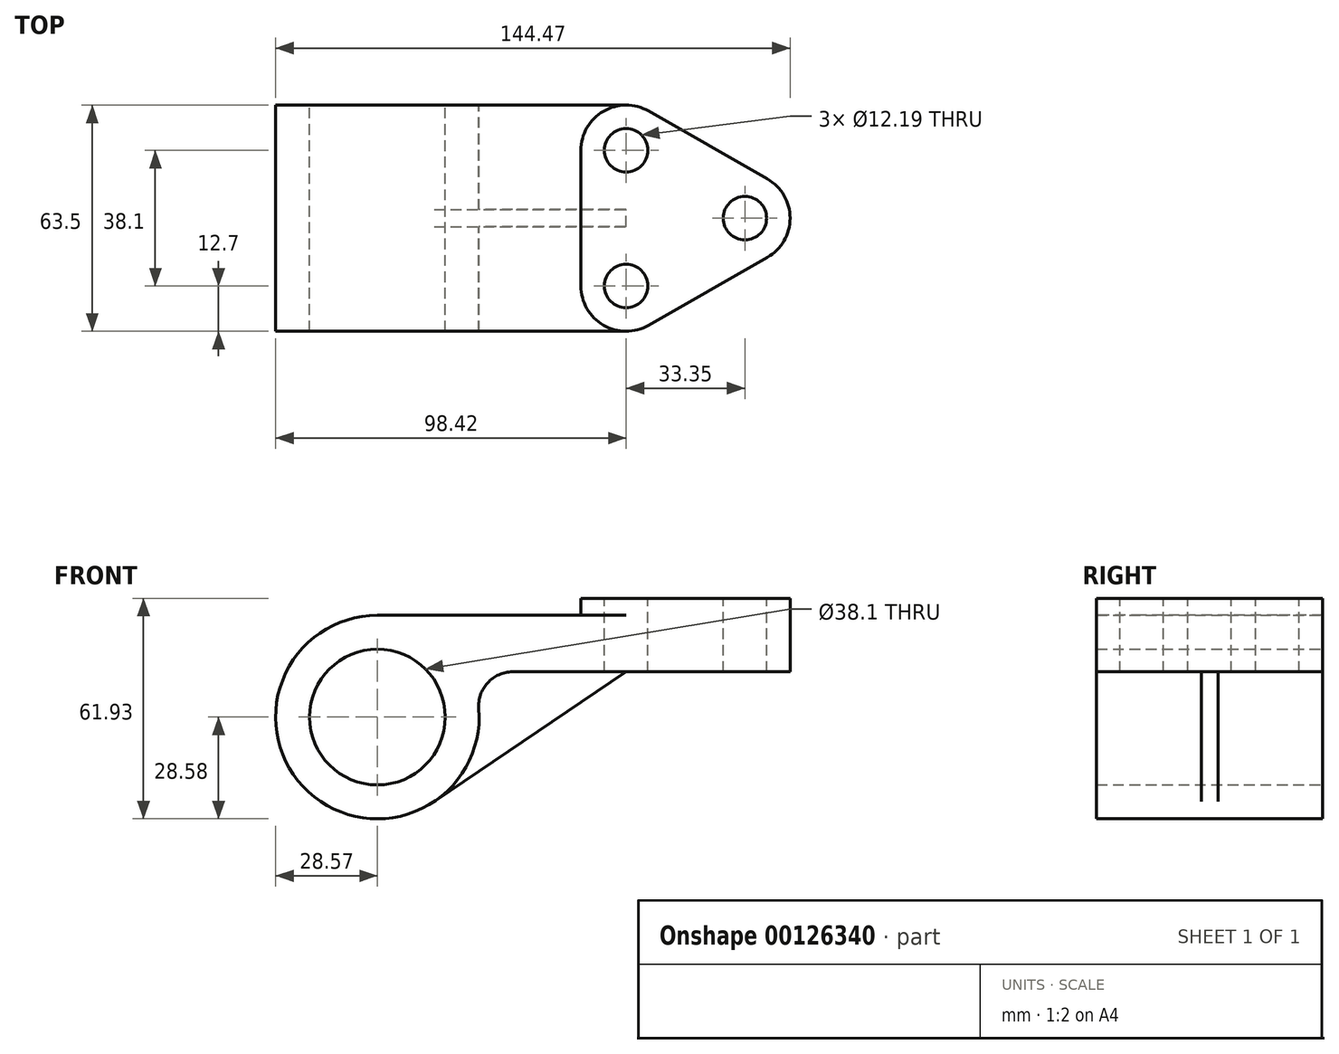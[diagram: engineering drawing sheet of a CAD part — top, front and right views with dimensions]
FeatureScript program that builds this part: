
annotation { "Feature Type Name" : "Feature", "Feature Type Description" : "" }
export const myFeature = defineFeature(function(context is Context, id is Id, definition is map)
    precondition{}
    {
        {
            var Q0;
            Q0=qCreatedBy(makeId("Front.planeOp"),FACE);
            var sketch = newSketch(context, id + "F0", { "sketchPlane" : qUnion([Q0])});
            skCircle(sketch, "E0", {"center": v(0, 0) * mm, "radius": 19.05 * mm});
            skArc(sketch, "E1", {"start": v(0, 28.58) * mm, "mid": v(-19.35, -21.03) * mm, "end": v(28.48, 2.38) * mm});
            skLineSegment(sketch, "E2", {"start": v(0, 28.58) * mm, "end": v(69.85, 28.58) * mm});
            skLineSegment(sketch, "E3", {"start": v(69.85, 28.58) * mm, "end": v(69.85, 12.7) * mm});
            skLineSegment(sketch, "E4", {"start": v(69.85, 12.7) * mm, "end": v(37.97, 12.7) * mm});
            skArc(sketch, "E5", {"start": v(37.97, 12.7) * mm, "mid": v(30.96, 9.62) * mm, "end": v(28.48, 2.38) * mm});
            skSolve(sketch);
        }
        {
            var Q0;
            Q0=qSketchRegion(id+"F0",true);
            extrude(context, id + "F1", {"entities" : qUnion([Q0]), "depth" : 63.5 * mm});
        }
        {
            var Q0;
            Q0=makeQuery(id+"F1.opExtrude","SWEPT_FACE",FACE,{"disambiguationData":[OSD([sQuery(id+"F0.wireOp",EDGE,"E2")])]});
            var sketch = newSketch(context, id + "F2", { "sketchPlane" : qUnion([Q0])});
            skLineSegment(sketch, "E6", {"start": v(0, 0) * mm, "end": v(97.46, 0) * mm, "construction": true});
            skLineSegment(sketch, "E7", {"start": v(0, -31.75) * mm, "end": v(120, -31.75) * mm, "construction": true});
            skPoint(sketch, "E7.endSnap0", {"position": v(0, -31.75) * mm});
            skArc(sketch, "E8", {"start": v(69.85, 0) * mm, "mid": v(60.87, -3.72) * mm, "end": v(57.15, -12.7) * mm});
            skLineSegment(sketch, "E9", {"start": v(57.15, -12.7) * mm, "end": v(57.15, -31.75) * mm});
            skArc(sketch, "E10", {"start": v(76.15, -1.67) * mm, "mid": v(73.1, -0.43) * mm, "end": v(69.85, 0) * mm});
            skLineSegment(sketch, "E11", {"start": v(76.15, -1.67) * mm, "end": v(109.5, -20.72) * mm});
            skArc(sketch, "E12", {"start": v(115.9, -31.75) * mm, "mid": v(114.18, -25.37) * mm, "end": v(109.5, -20.72) * mm});
            skArc(sketch, "E13.MirrorCS", {"start": v(115.9, -31.75) * mm, "mid": v(114.18, -38.13) * mm, "end": v(109.5, -42.78) * mm});
            skLineSegment(sketch, "E14.MirrorCS", {"start": v(76.15, -61.83) * mm, "end": v(109.5, -42.78) * mm});
            skArc(sketch, "E15.MirrorCS", {"start": v(76.15, -61.83) * mm, "mid": v(73.1, -63.07) * mm, "end": v(69.85, -63.5) * mm});
            skLineSegment(sketch, "E16.MirrorCS", {"start": v(57.15, -50.8) * mm, "end": v(57.15, -31.75) * mm});
            skArc(sketch, "E17.MirrorCS", {"start": v(69.85, -63.5) * mm, "mid": v(60.87, -59.78) * mm, "end": v(57.15, -50.8) * mm});
            skSolve(sketch);
        }
        {
            var Q0;
            Q0=qSketchRegion(id+"F2",true);
            var Q1;
            Q1=makeQuery(id+"F1.opExtrude","SWEPT_FACE",FACE,{"disambiguationData":[OSD([sQuery(id+"F0.wireOp",EDGE,"E4")])]});
            extrude(context, id + "F3", {"entities" : qUnion([Q0]), "operationType" : NewBodyOperationType.ADD, "endBound" : BoundingType.UP_TO_SURFACE, "oppositeDirection" : true, "endBoundEntityFace" : qUnion([Q1]), "depth" : 25.4 * mm, "hasSecondDirection" : true, "secondDirectionOppositeDirection" : false, "secondDirectionDepth" : 4.78 * mm});
        }
        {
            var Q0;
            Q0=makeQuery(id+"F3.opExtrude","CAP_FACE",FACE,{"disambiguationData":[OSD([sQuery(id+"F2.wireOp",EDGE,"E8"),sQuery(id+"F2.wireOp",EDGE,"E9"),sQuery(id+"F2.wireOp",EDGE,"E10"),sQuery(id+"F2.wireOp",EDGE,"E11"),sQuery(id+"F2.wireOp",EDGE,"E12"),sQuery(id+"F2.wireOp",EDGE,"E13.MirrorCS"),sQuery(id+"F2.wireOp",EDGE,"E14.MirrorCS"),sQuery(id+"F2.wireOp",EDGE,"E15.MirrorCS"),sQuery(id+"F2.wireOp",EDGE,"E16.MirrorCS"),sQuery(id+"F2.wireOp",EDGE,"E17.MirrorCS")])],"isStart":true});
            var sketch = newSketch(context, id + "F4", { "sketchPlane" : qUnion([Q0])});
            skCircle(sketch, "E18", {"center": v(69.85, -12.7) * mm, "radius": 6.1 * mm});
            skCircle(sketch, "E19", {"center": v(69.85, -50.8) * mm, "radius": 6.1 * mm});
            skCircle(sketch, "E20", {"center": v(103.2, -31.75) * mm, "radius": 6.1 * mm});
            skSolve(sketch);
        }
        {
            var Q0;
            Q0=qSketchRegion(id+"F4",true);
            extrude(context, id + "F5", {"entities" : qUnion([Q0]), "operationType" : NewBodyOperationType.REMOVE, "endBound" : BoundingType.THROUGH_ALL, "oppositeDirection" : true, "depth" : 25.4 * mm});
        }
        {
            var Q0;
            Q0=qCreatedBy(makeId("Front.planeOp"),FACE);
            cPlane(context, id + "F6", {"entities" : qUnion([Q0]), "cplaneType" : CPlaneType.OFFSET, "offset" : 31.75 * mm, "width" : 152.4 * mm, "height" : 152.4 * mm});
        }
        {
            var Q0;
            Q0=qCreatedBy(id+"F6.planeOp",FACE);
            var sketch = newSketch(context, id + "F7", { "sketchPlane" : qUnion([Q0])});
            skLineSegment(sketch, "E21", {"start": v(16, -23.68) * mm, "end": v(69.85, 12.7) * mm});
            skArc(sketch, "E22.0", {"start": v(16, -23.68) * mm, "mid": v(25.77, -12.34) * mm, "end": v(28.48, 2.38) * mm});
            skArc(sketch, "E22.1", {"start": v(37.97, 12.7) * mm, "mid": v(30.96, 9.62) * mm, "end": v(28.48, 2.38) * mm});
            skLineSegment(sketch, "E22.2", {"start": v(69.85, 12.7) * mm, "end": v(37.97, 12.7) * mm});
            skPoint(sketch, "E23.orphan", {"position": v(0, 28.58) * mm});
            skSolve(sketch);
        }
        {
            var Q0;
            Q0=qSketchRegion(id+"F7",true);
            extrude(context, id + "F8", {"entities" : qUnion([Q0]), "operationType" : NewBodyOperationType.ADD, "endBound" : BoundingType.SYMMETRIC, "depth" : 4.76 * mm});
        }
    });
